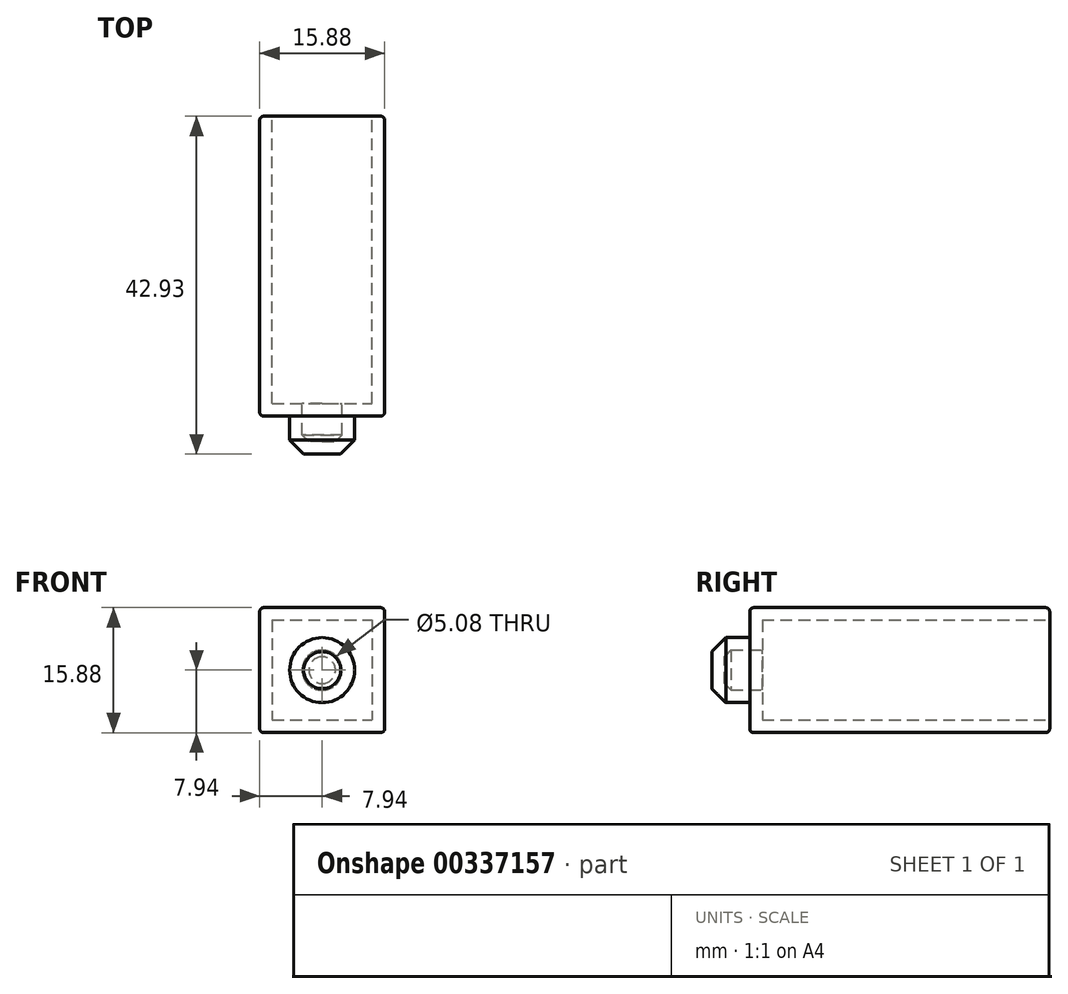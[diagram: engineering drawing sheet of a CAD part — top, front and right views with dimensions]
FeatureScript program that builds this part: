
annotation { "Feature Type Name" : "Feature", "Feature Type Description" : "" }
export const myFeature = defineFeature(function(context is Context, id is Id, definition is map)
    precondition{}
    {
        {
            var Q0;
            Q0=qCreatedBy(makeId("Front.planeOp"),FACE);
            var sketch = newSketch(context, id + "F0", { "sketchPlane" : qUnion([Q0])});
            skLineSegment(sketch, "E0.bottom", {"start": v(-7.94, 7.94) * mm, "end": v(7.94, 7.94) * mm});
            skLineSegment(sketch, "E0.top", {"start": v(-7.94, -7.94) * mm, "end": v(7.94, -7.94) * mm});
            skLineSegment(sketch, "E0.left", {"start": v(-7.94, 7.94) * mm, "end": v(-7.94, -7.94) * mm});
            skLineSegment(sketch, "E0.right", {"start": v(7.94, 7.94) * mm, "end": v(7.94, -7.94) * mm});
            skPoint(sketch, "E0.middle", {"position": v(0, 0) * mm});
            skSolve(sketch);
        }
        {
            var Q0;
            Q0=qSketchRegion(id+"F0",true);
            extrude(context, id + "F1", {"entities" : qUnion([Q0]), "depth" : 38.1 * mm});
        }
        {
            var Q0;
            Q0=makeQuery(id+"F1.opExtrude","CAP_FACE",FACE,{"disambiguationData":[OSD([sQuery(id+"F0.wireOp",EDGE,"E0.bottom"),sQuery(id+"F0.wireOp",EDGE,"E0.top"),sQuery(id+"F0.wireOp",EDGE,"E0.left"),sQuery(id+"F0.wireOp",EDGE,"E0.right")])],"isStart":false});
            var sketch = newSketch(context, id + "F2", { "sketchPlane" : qUnion([Q0])});
            skCircle(sketch, "E1", {"center": v(0, 0) * mm, "radius": 4.13 * mm});
            skSolve(sketch);
        }
        {
            var Q0;
            Q0=qSketchRegion(id+"F2",true);
            extrude(context, id + "F3", {"entities" : qUnion([Q0]), "operationType" : NewBodyOperationType.ADD, "depth" : 4.83 * mm});
        }
        {
            var Q0;
            Q0=makeQuery(id+"F3.opExtrude","CAP_FACE",FACE,{"disambiguationData":[OSD([sQuery(id+"F2.wireOp",EDGE,"E1")])],"isStart":false});
            chamfer(context, id + "F4", {"entities" : qUnion([Q0]), "width" : 1.78 * mm, "tangentPropagation" : true});
        }
        {
            var Q0;
            Q0=makeQuery(id+"F1.opExtrude","CAP_FACE",FACE,{"disambiguationData":[OSD([sQuery(id+"F0.wireOp",EDGE,"E0.bottom"),sQuery(id+"F0.wireOp",EDGE,"E0.top"),sQuery(id+"F0.wireOp",EDGE,"E0.left"),sQuery(id+"F0.wireOp",EDGE,"E0.right")])],"isStart":true});
            shell(context, id + "F5", {"entities" : qUnion([Q0]), "thickness" : 1.59 * mm});
        }
        {
            var Q0;
            Q0=makeQuery(id+"F1.opExtrude","CAP_EDGE",EDGE,{"disambiguationData":[OSD([sQuery(id+"F0.wireOp",EDGE,"E0.bottom")])],"isStart":false});
            var Q1;
            Q1=makeQuery(id+"F1.opExtrude","CAP_EDGE",EDGE,{"disambiguationData":[OSD([sQuery(id+"F0.wireOp",EDGE,"E0.left")])],"isStart":false});
            var Q2;
            Q2=makeQuery(id+"F1.opExtrude","CAP_EDGE",EDGE,{"disambiguationData":[OSD([sQuery(id+"F0.wireOp",EDGE,"E0.top")])],"isStart":false});
            var Q3;
            Q3=makeQuery(id+"F1.opExtrude","CAP_EDGE",EDGE,{"disambiguationData":[OSD([sQuery(id+"F0.wireOp",EDGE,"E0.right")])],"isStart":false});
            var Q4;
            Q4=makeQuery(id+"F1.opExtrude","SWEPT_EDGE",EDGE,{"disambiguationData":[OSD([sQuery(id+"F0.wireOp",EDGE,"E0.bottom"),sQuery(id+"F0.wireOp",EDGE,"E0.left")])]});
            var Q5;
            Q5=makeQuery(id+"F1.opExtrude","SWEPT_EDGE",EDGE,{"disambiguationData":[OSD([sQuery(id+"F0.wireOp",EDGE,"E0.top"),sQuery(id+"F0.wireOp",EDGE,"E0.left")])]});
            var Q6;
            Q6=makeQuery(id+"F1.opExtrude","SWEPT_EDGE",EDGE,{"disambiguationData":[OSD([sQuery(id+"F0.wireOp",EDGE,"E0.bottom"),sQuery(id+"F0.wireOp",EDGE,"E0.right")])]});
            var Q7;
            Q7=makeQuery(id+"F1.opExtrude","SWEPT_EDGE",EDGE,{"disambiguationData":[OSD([sQuery(id+"F0.wireOp",EDGE,"E0.top"),sQuery(id+"F0.wireOp",EDGE,"E0.right")])]});
            var Q8;
            Q8=makeQuery(id+"F1.opExtrude","CAP_EDGE",EDGE,{"disambiguationData":[OSD([sQuery(id+"F0.wireOp",EDGE,"E0.top")])],"isStart":true});
            var Q9;
            Q9=makeQuery(id+"F1.opExtrude","CAP_EDGE",EDGE,{"disambiguationData":[OSD([sQuery(id+"F0.wireOp",EDGE,"E0.right")])],"isStart":true});
            var Q10;
            Q10=makeQuery(id+"F1.opExtrude","CAP_EDGE",EDGE,{"disambiguationData":[OSD([sQuery(id+"F0.wireOp",EDGE,"E0.bottom")])],"isStart":true});
            var Q11;
            Q11=makeQuery(id+"F1.opExtrude","CAP_EDGE",EDGE,{"disambiguationData":[OSD([sQuery(id+"F0.wireOp",EDGE,"E0.left")])],"isStart":true});
            fillet(context, id + "F6", {"entities" : qUnion([Q0, Q1, Q2, Q3, Q4, Q5, Q6, Q7, Q8, Q9, Q10, Q11]), "radius" : 0.5 * mm, "tangentPropagation" : true, "allowEdgeOverflow" : false});
        }
    });
